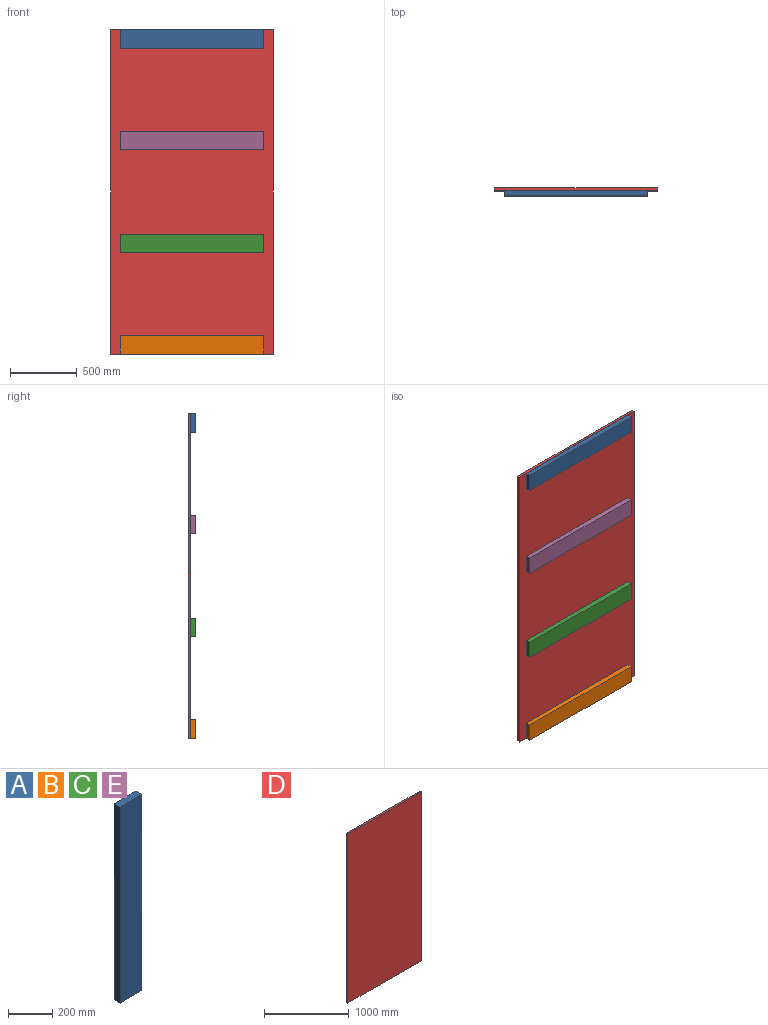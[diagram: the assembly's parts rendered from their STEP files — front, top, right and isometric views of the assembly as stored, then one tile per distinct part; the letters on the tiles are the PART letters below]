
ASSEMBLY  parts=5 mates=4
PART A: 6 faces, bbox 139.7x38.1x1079.5 mm
  f0: plane 139.7x38.1mm, normal (0,0,1), area 5322.6mm2, adj f1,f3,f4,f5
  f1: plane 1079.5x38.1mm, normal (-1,0,0), area 41128.9mm2, adj f0,f2,f4,f5
  f2: plane 139.7x38.1mm, normal (0,0,-1), area 5322.6mm2, adj f1,f3,f4,f5
  f3: plane 1079.5x38.1mm, normal (1,0,0), area 41128.9mm2, adj f0,f2,f4,f5
  f4: plane 1079.5x139.7mm, normal (0,-1,0), area 150806.1mm2, adj f0,f1,f2,f3
  f5: plane 1079.5x139.7mm, normal (0,1,0), area 150806.1mm2, adj f0,f1,f2,f3
PART B: same geometry as A
PART C: same geometry as A
PART D: 6 faces, bbox 1219.2x19.1x2438.4 mm
  f0: plane 1219.2x19.05mm, normal (0,0,1), area 23225.8mm2, adj f1,f3,f4,f5
  f1: plane 2438.4x19.05mm, normal (-1,0,0), area 46451.5mm2, adj f0,f2,f4,f5
  f2: plane 1219.2x19.05mm, normal (0,0,-1), area 23225.8mm2, adj f1,f3,f4,f5
  f3: plane 2438.4x19.05mm, normal (1,0,0), area 46451.5mm2, adj f0,f2,f4,f5
  f4: plane 2438.4x1219.2mm, normal (0,-1,0), area 2972897.3mm2, adj f0,f1,f2,f3
  f5: plane 2438.4x1219.2mm, normal (0,1,0), area 2972897.3mm2, adj f0,f1,f2,f3
PART E: same geometry as A
PLACE A rot(axis=(0.71,0,0.71),180deg) t=(-1139.73,-51.95,1771.31)mm
PLACE B rot(axis=(0.71,0,0.71),180deg) t=(-1139.73,-51.95,-527.39)mm
PLACE C rot(axis=(0.71,0,0.71),180deg) t=(-1139.73,-51.95,234.61)mm
PLACE D t=(-730.47,5.2,-175.97)mm
PLACE E rot(axis=(0.71,0,0.71),180deg) t=(-1139.73,-51.95,1009.31)mm
MATE fastened E.f4 <-> D.f4  axis (0,1,0) through (-733.05,-13.85,1015.7)mm
MATE fastened C.f4 <-> D.f4  axis (0,1,0) through (-733.05,-13.85,241)mm
MATE fastened A.f4 <-> D.f4  axis (0,1,0) through (-733.05,-13.85,1777.7)mm
MATE fastened B.f4 <-> D.f4  axis (0,1,0) through (-733.05,-13.85,-521)mm
